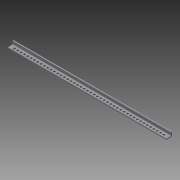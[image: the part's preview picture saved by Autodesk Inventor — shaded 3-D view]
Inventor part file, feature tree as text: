
AUTODESK INVENTOR PART (.ipt)
format: ipt  version: 2013 (Build 170138000, 138)  size: 217,088 bytes
history: native  units: in
note: dims shown in document units (in); Inventor stores cm internally (conversion verified against a paired STEP export)
features: sheet_metal_op x4, other x3, sketch x2
ambient origin geometry x8: Origin, YZ Plane, XZ Plane, XY Plane, X Axis, Y Axis, Z Axis, Center Point
bodies: Solid1 (feature_tree)
feature tree (9):
  sheet_metal_op  "Face1"
  sheet_metal_op  "Flange1"
  sketch  "Sketch1"  dims[d0=0.125in]
  other  "Plate1"
  sketch  "Sketch2"  dims[d1=0.125in d2=0.0625in d3=0.25in d4=0.125in d5=0.5in d6=90.0deg d7=0.05in d8=0.5in d9=0.125in d10=0.125in]
  other  "Plate2"
  sheet_metal_op  "Bend1"
  sheet_metal_op  "Corner1"
  other  "Definition1"
